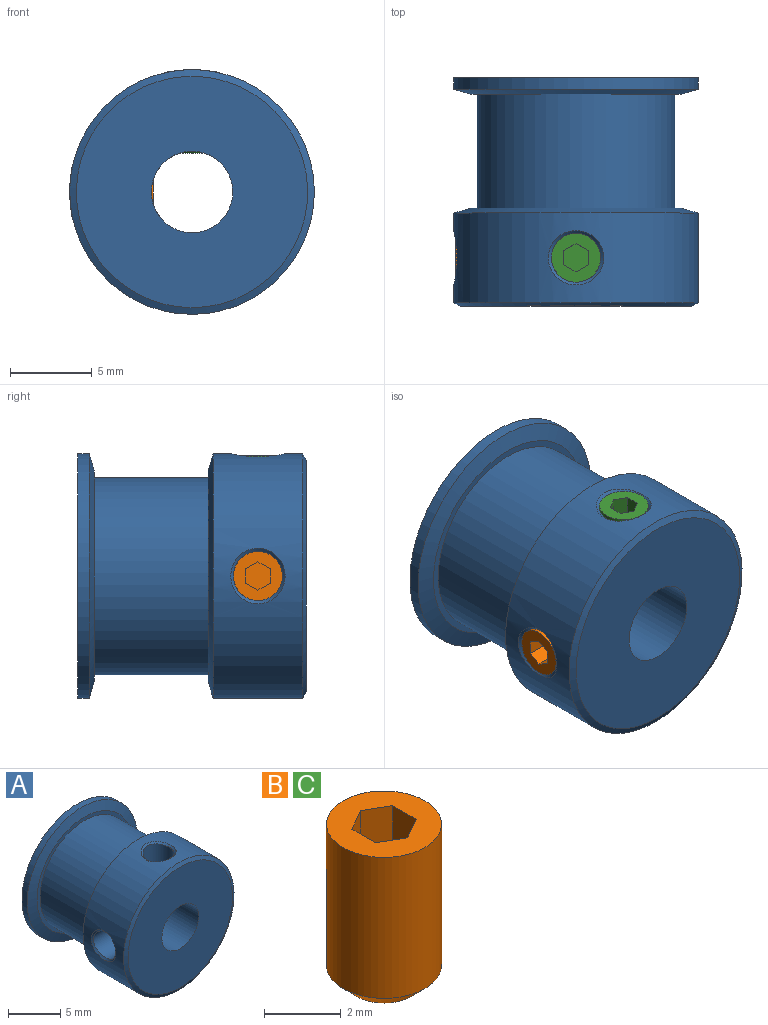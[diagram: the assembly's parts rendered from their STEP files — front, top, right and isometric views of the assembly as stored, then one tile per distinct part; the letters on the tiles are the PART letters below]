
ASSEMBLY  parts=3 mates=2
PART A: 17 faces, bbox 15x14x15 mm
  f0: cylinder r=7.5mm len=15mm, axis (0,-1,0), area 241.2mm2, adj f2,f3,f15,f16
  f1: plane 14.18x14.18mm, normal (0,-1,0), area 138.2mm2, adj f2,f12
  f2: cone r=7.5mm half-angle=63.4deg, axis (0,1,0), area 21.1mm2, adj f0,f1
  f3: cone r=7.5mm half-angle=74.3deg, axis (0,-1,0), area 47.4mm2, adj f0,f4
  f4: plane 12.92x12.92mm, normal (0,1,0), area 16.1mm2, adj f3,f5
  f5: cylinder r=6.05mm len=12.1mm, axis (0,-1,0), area 266.1mm2, adj f4,f6
  f6: plane 12.92x12.92mm, normal (0,-1,0), area 16.1mm2, adj f5,f7
  f7: cone r=7.5mm half-angle=73.9deg, axis (0,1,0), area 47.5mm2, adj f6,f8
  f8: cylinder r=7.5mm len=15mm, axis (0,-1,0), area 33mm2, adj f7,f9
  f9: cone r=4.25mm half-angle=86.8deg, axis (0,1,0), area 120.2mm2, adj f8,f10
  f10: cone r=4.17mm half-angle=23.1deg, axis (0,-1,0), area 5.3mm2, adj f9,f11
  f11: plane 8.34x8.34mm, normal (0,1,0), area 35mm2, adj f10,f12
  f12: cylinder r=2.5mm len=14mm, axis (0,-1,0), area 205.1mm2, adj f1,f11,f13,f14
  f13: cylinder r=1.5mm len=5.15mm, axis (0,0,-1), area 48.5mm2, adj f12,f15
  f14: cylinder r=1.5mm len=5.15mm, axis (1,0,0), area 48.5mm2, adj f12,f16
  f15: bspline ~3.4x3.33mm, area 2.4mm2, adj f0,f13
  f16: bspline ~3.4x3.33mm, area 2.4mm2, adj f0,f14
PART B: 11 faces, bbox 3x3x5 mm
  f0: plane 3x3mm, normal (0,0,1), area 5.1mm2, adj f1,f3,f4,f5,f6,f7,f8
  f1: cylinder r=1.5mm len=4.5mm, axis (0,0,-1), area 42.4mm2, adj f0,f10
  f2: plane 2x2mm, normal (0,0,-1), area 3.1mm2, adj f10
  f3: plane 1.5x0.87mm, normal (-1,0,0), area 1.3mm2, adj f0,f4,f8,f9
  f4: plane 1.5x0.75mm, normal (-0.5,-0.87,0), area 1.3mm2, adj f0,f3,f5,f9
  f5: plane 1.5x0.75mm, normal (0.5,-0.87,0), area 1.3mm2, adj f0,f4,f6,f9
  f6: plane 1.5x0.87mm, normal (1,0,0), area 1.3mm2, adj f0,f5,f7,f9
  f7: plane 1.5x0.75mm, normal (0.5,0.87,0), area 1.3mm2, adj f0,f6,f8,f9
  f8: plane 1.5x0.75mm, normal (-0.5,0.87,0), area 1.3mm2, adj f0,f3,f7,f9
  f9: plane 1.73x1.5mm, normal (0,0,1), area 1.9mm2, adj f3,f4,f5,f6,f7,f8
  f10: cone r=1.5mm half-angle=45deg, axis (0,0,1), area 5.6mm2, adj f1,f2
PART C: same geometry as B
PLACE A at identity
PLACE B rot(axis=(-0.58,-0.58,0.58),120deg) t=(-2.37,2.96,0)mm
PLACE C t=(0,2.96,2.37)mm
MATE fastened C.f1 <-> A.f13  axis (0,0,-1) through (0,2.96,7.37)mm
MATE fastened B.f1 <-> A.f14  axis (1,0,0) through (-7.37,2.96,0)mm
